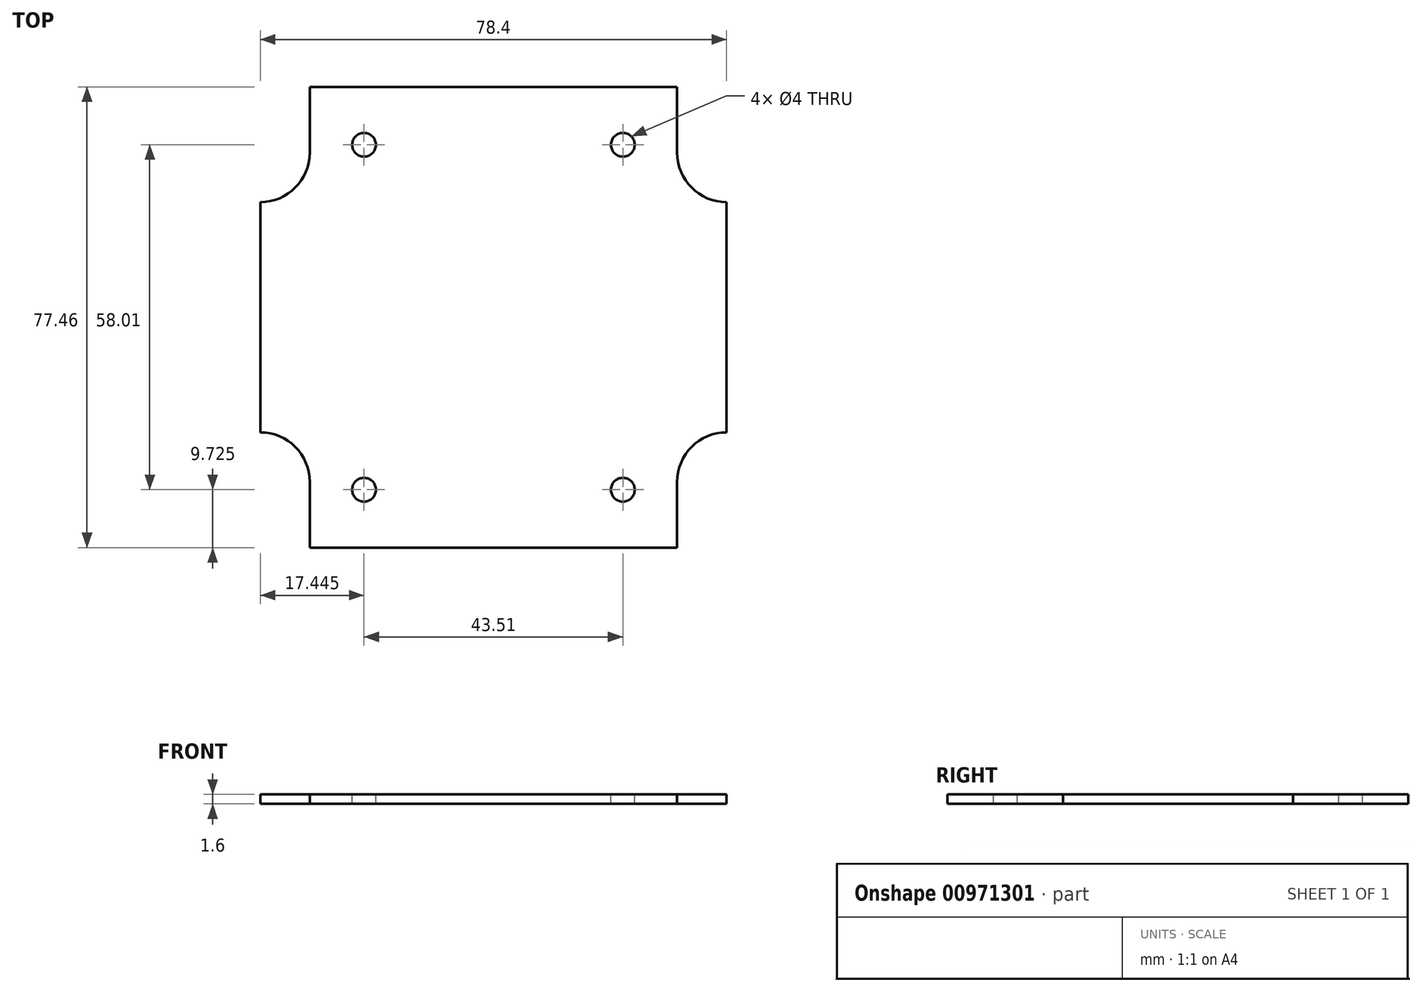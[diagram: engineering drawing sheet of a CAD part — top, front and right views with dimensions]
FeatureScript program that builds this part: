
annotation { "Feature Type Name" : "Feature", "Feature Type Description" : "" }
export const myFeature = defineFeature(function(context is Context, id is Id, definition is map)
    precondition{}
    {
        {
            var Q0;
            Q0=qCreatedBy(makeId("Top.planeOp"),FACE);
            var sketch = newSketch(context, id + "F0", { "sketchPlane" : qUnion([Q0])});
            skLineSegment(sketch, "E0", {"start": v(-30.87, 38.73) * mm, "end": v(30.88, 38.74) * mm});
            skLineSegment(sketch, "E1", {"start": v(30.88, 38.74) * mm, "end": v(30.88, 27.69) * mm});
            skLineSegment(sketch, "E2", {"start": v(39.2, 19.36) * mm, "end": v(39.2, 19.36) * mm});
            skLineSegment(sketch, "E3", {"start": v(39.2, 19.36) * mm, "end": v(39.2, -19.35) * mm});
            skLineSegment(sketch, "E4", {"start": v(39.2, -19.35) * mm, "end": v(39.2, -19.35) * mm});
            skLineSegment(sketch, "E5", {"start": v(30.88, -27.68) * mm, "end": v(30.88, -38.73) * mm});
            skLineSegment(sketch, "E6", {"start": v(30.88, -38.73) * mm, "end": v(-30.87, -38.74) * mm});
            skLineSegment(sketch, "E7", {"start": v(-30.87, -38.74) * mm, "end": v(-30.87, -27.69) * mm});
            skLineSegment(sketch, "E8", {"start": v(-39.2, -19.36) * mm, "end": v(-39.2, -19.36) * mm});
            skLineSegment(sketch, "E9", {"start": v(-39.2, -19.36) * mm, "end": v(-39.2, 19.35) * mm});
            skLineSegment(sketch, "E10", {"start": v(-39.2, 19.35) * mm, "end": v(-39.2, 19.35) * mm});
            skLineSegment(sketch, "E11", {"start": v(-30.87, 27.68) * mm, "end": v(-30.87, 38.73) * mm});
            skPoint(sketch, "E12.visualSharp", {"position": v(-30.87, 19.35) * mm});
            skArc(sketch, "E12.filletArc", {"start": v(-39.2, 19.35) * mm, "mid": v(-33.31, 21.8) * mm, "end": v(-30.87, 27.68) * mm});
            skPoint(sketch, "E13.visualSharp", {"position": v(30.88, 19.36) * mm});
            skArc(sketch, "E13.filletArc", {"start": v(30.88, 27.69) * mm, "mid": v(33.31, 21.8) * mm, "end": v(39.2, 19.36) * mm});
            skPoint(sketch, "E14.visualSharp", {"position": v(30.88, -19.35) * mm});
            skArc(sketch, "E14.filletArc", {"start": v(39.2, -19.35) * mm, "mid": v(33.31, -21.8) * mm, "end": v(30.88, -27.68) * mm});
            skPoint(sketch, "E15.visualSharp", {"position": v(-30.87, -19.36) * mm});
            skArc(sketch, "E15.filletArc", {"start": v(-30.87, -27.69) * mm, "mid": v(-33.31, -21.8) * mm, "end": v(-39.2, -19.36) * mm});
            skSolve(sketch);
        }
        {
            var Q0;
            Q0=makeQuery(id+"F0.imprint","IMPRINT",FACE,{"disambiguationData":[TD([[makeQuery(id+"F0.imprint","IMPRINT",EDGE,{"derivedFrom":sQuery(id+"F0.wireOp",EDGE,"E0")}),-1.0]])]});
            extrude(context, id + "F1", {"entities" : qUnion([Q0]), "depth" : 1.6 * mm, "offsetDistance" : 25 * mm});
        }
        {
            var Q0;
            Q0=makeQuery(id+"F1.opExtrude","CAP_FACE",FACE,{"disambiguationData":[OSD([sQuery(id+"F0.wireOp",EDGE,"E0"),sQuery(id+"F0.wireOp",EDGE,"E1"),sQuery(id+"F0.wireOp",EDGE,"E3"),sQuery(id+"F0.wireOp",EDGE,"E5"),sQuery(id+"F0.wireOp",EDGE,"E6"),sQuery(id+"F0.wireOp",EDGE,"E7"),sQuery(id+"F0.wireOp",EDGE,"E9"),sQuery(id+"F0.wireOp",EDGE,"E11"),sQuery(id+"F0.wireOp",EDGE,"E12.filletArc"),sQuery(id+"F0.wireOp",EDGE,"E13.filletArc"),sQuery(id+"F0.wireOp",EDGE,"E14.filletArc"),sQuery(id+"F0.wireOp",EDGE,"E15.filletArc")])],"isStart":false});
            var sketch = newSketch(context, id + "F2", { "sketchPlane" : qUnion([Q0])});
            skCircle(sketch, "E16", {"center": v(-21.75, 29) * mm, "radius": 2 * mm});
            skCircle(sketch, "E17", {"center": v(21.75, 29) * mm, "radius": 2 * mm});
            skCircle(sketch, "E18", {"center": v(-21.75, -29) * mm, "radius": 2 * mm});
            skCircle(sketch, "E19", {"center": v(21.75, -29) * mm, "radius": 2 * mm});
            skSolve(sketch);
        }
        {
            var Q0;
            Q0 = qSketchRegion(id + "F2", true);
            extrude(context, id + "F3", {"entities" : qUnion([Q0]), "operationType" : NewBodyOperationType.REMOVE, "oppositeDirection" : true, "depth" : 25 * mm, "offsetDistance" : 25 * mm});
        }
    });
